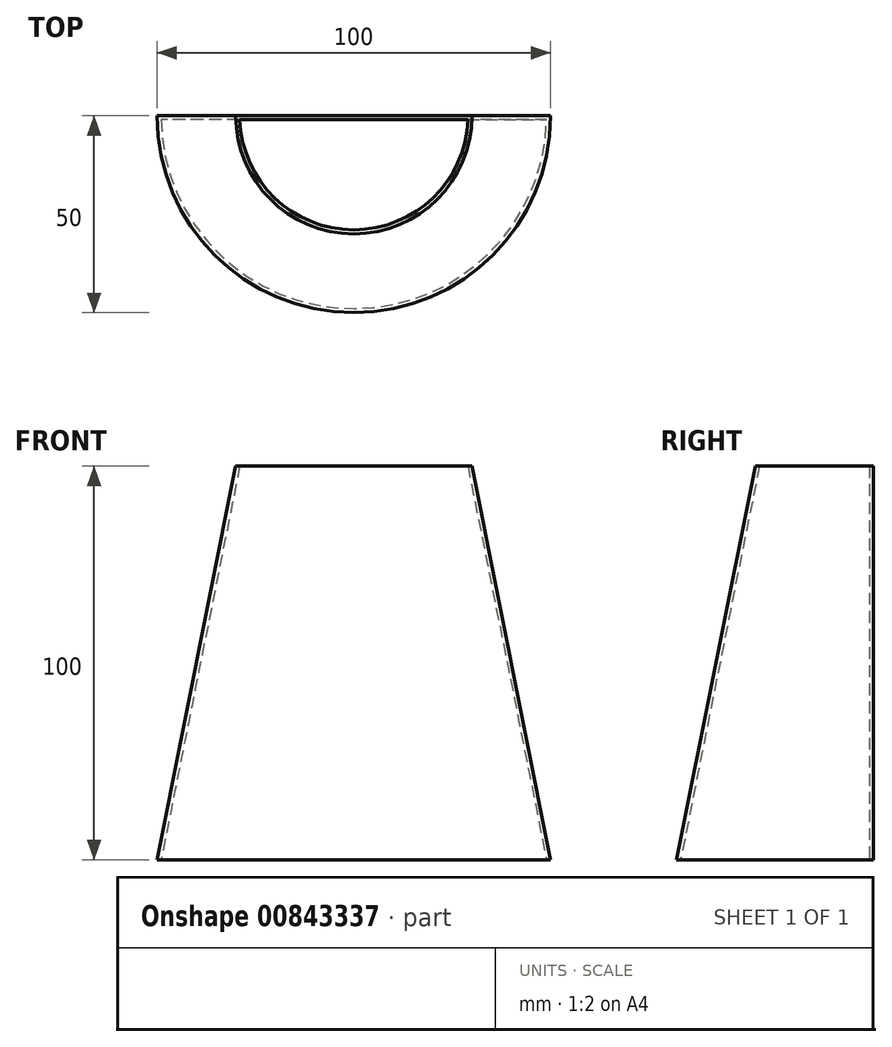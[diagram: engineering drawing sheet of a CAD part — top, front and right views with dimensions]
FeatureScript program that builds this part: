
annotation { "Feature Type Name" : "Feature", "Feature Type Description" : "" }
export const myFeature = defineFeature(function(context is Context, id is Id, definition is map)
    precondition{}
    {
        {
            var Q0;
            Q0=qCreatedBy(makeId("Front.planeOp"),FACE);
            var sketch = newSketch(context, id + "F0", { "sketchPlane" : qUnion([Q0])});
            skLineSegment(sketch, "E0", {"start": v(0, 0) * mm, "end": v(0, 100) * mm});
            skLineSegment(sketch, "E1", {"start": v(0, 100) * mm, "end": v(-30, 100) * mm});
            skLineSegment(sketch, "E2", {"start": v(-30, 100) * mm, "end": v(-50, 0) * mm});
            skLineSegment(sketch, "E3", {"start": v(-50, 0) * mm, "end": v(0, 0) * mm});
            skSolve(sketch);
        }
        {
            var Q0;
            Q0=makeQuery(id+"F0.imprint","IMPRINT",FACE,{"disambiguationData":[TD([[makeQuery(id+"F0.imprint","IMPRINT",EDGE,{"derivedFrom":sQuery(id+"F0.wireOp",EDGE,"E0")}),1.0]])]});
            var Q1;
            Q1=sQuery(id+"F0.wireOp",EDGE,"E0");
            revolve(context, id + "F1", {"surfaceOperationType" : NewSurfaceOperationType.NEW, "entities" : qUnion([Q0]), "axis" : qUnion([Q1]), "revolveType" : RevolveType.ONE_DIRECTION, "angle" : 180 * degree});
        }
        {
            var Q0;
            Q0=makeQuery(id+"F1.opRevolve","SWEPT_FACE",FACE,{"disambiguationData":[OSD([sQuery(id+"F0.wireOp",EDGE,"E1")])]});
            var Q1;
            Q1=makeQuery(id+"F1.opRevolve","CAP_FACE",FACE,{"disambiguationData":[OSD([sQuery(id+"F0.wireOp",EDGE,"E0"),sQuery(id+"F0.wireOp",EDGE,"E1"),sQuery(id+"F0.wireOp",EDGE,"E2"),sQuery(id+"F0.wireOp",EDGE,"E3")])],"isStart":false});
            var Q2;
            Q2=makeQuery(id+"F1.opRevolve","SWEPT_FACE",FACE,{"disambiguationData":[OSD([sQuery(id+"F0.wireOp",EDGE,"E3")])]});
            shell(context, id + "F2", {"entities" : qUnion([Q0, Q1, Q2]), "thickness" : 1 * mm});
        }
    });
